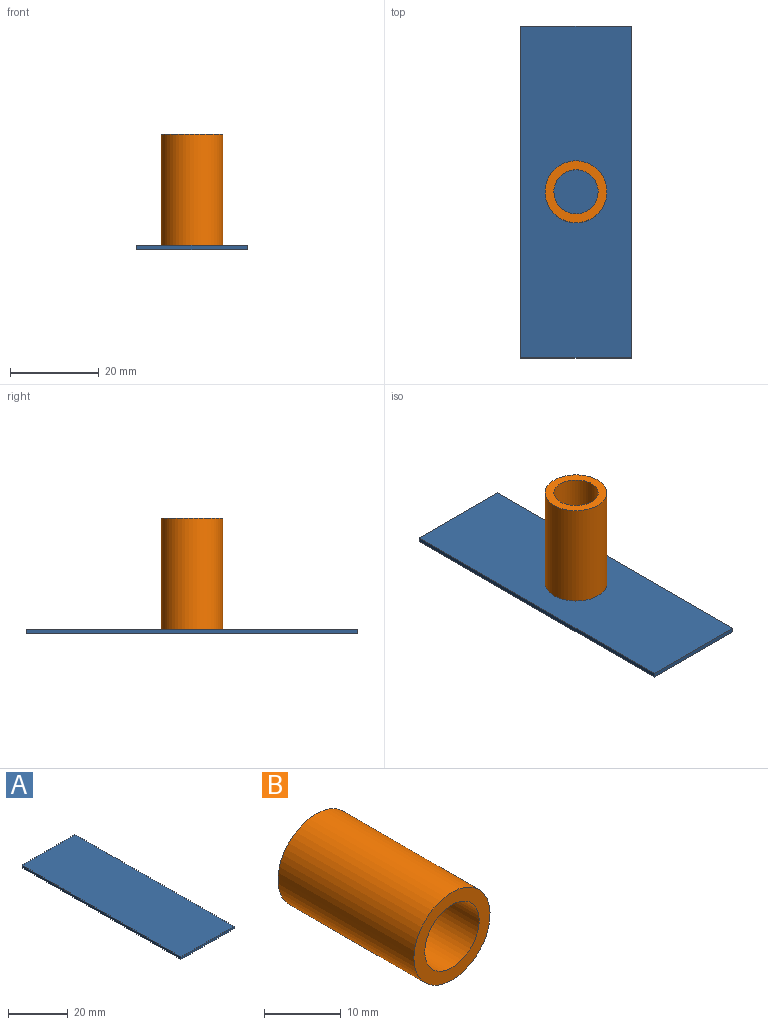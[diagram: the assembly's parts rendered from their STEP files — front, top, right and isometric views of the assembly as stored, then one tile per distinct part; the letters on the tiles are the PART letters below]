
ASSEMBLY  parts=2 mates=1
PART A: 6 faces, bbox 25x75x1 mm
  f0: plane 75x1mm, normal (-1,0,0), area 75mm2, adj f1,f3,f4,f5
  f1: plane 75x25mm, normal (0,0,-1), area 1875mm2, adj f0,f2,f4,f5
  f2: plane 75x1mm, normal (1,0,0), area 75mm2, adj f1,f3,f4,f5
  f3: plane 75x25mm, normal (0,0,1), area 1875mm2, adj f0,f2,f4,f5
  f4: plane 25x1mm, normal (0,-1,0), area 25mm2, adj f0,f1,f2,f3
  f5: plane 25x1mm, normal (0,1,0), area 25mm2, adj f0,f1,f2,f3
PART B: 4 faces, bbox 14x25x14 mm
  f0: cylinder r=5mm len=25mm, axis (0,1,0), area 785.4mm2, adj f2,f3
  f1: cylinder r=7mm len=25mm, axis (0,1,0), area 1099.6mm2, adj f2,f3
  f2: plane 14x14mm, normal (0,-1,0), area 75.4mm2, adj f0,f1
  f3: plane 14x14mm, normal (0,1,0), area 75.4mm2, adj f0,f1
PLACE A t=(-19.37,19.51,-21.53)mm
PLACE B rot(axis=(1,0,0),90deg) t=(-6.87,-17.99,4.47)mm
MATE parallel B.f1 <-> A.f3  axis (0,0,-1) through (-6.87,-17.99,-20.53)mm
